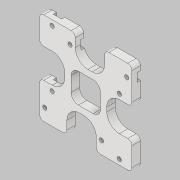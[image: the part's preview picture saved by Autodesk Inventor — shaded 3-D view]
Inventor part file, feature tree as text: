
AUTODESK INVENTOR PART (.ipt)
format: ipt  version: 2019.2 (Build 232265000, 265)  size: 918,016 bytes
history: native  units: mm
features: fillet x4, other x2, extrude x2, sketch x2
ambient origin geometry x8: Origin, YZ Plane, XZ Plane, XY Plane, X Axis, Y Axis, Z Axis, Center Point
bodies: Body1 (feature_tree)
feature tree (10):
  other  "BaseBottom"
  extrude  "Base"  Depth=12.0mm
  fillet  "Rundung1"  Radius=5.0mm
  fillet  "Rundung2"  Radius=14.0mm
  extrude  "Extrusion3"  Depth=3.0mm
  fillet  "Rundung3"  Radius=4.0mm
  fillet  "Rundung4"  Radius=3.5mm
  sketch  "Skizze2"  dims[d9=32.0mm d10=12.0mm d11=5.0mm d12=14.0mm]
  sketch  "Skizze4"  dims[d13=2.0mm d14=32.0mm d15=12.0mm d16=5.0mm d17=14.0mm d18=2.0mm d19=32.0mm d20=12.0mm d21=5.0mm d22=14.0mm d23=2.0mm d24=32.0mm d25=12.0mm d26=5.0mm d27=14.0mm d28=2.0mm d29=3.0mm d30=4.0mm d31=0.0mm d32=3.5mm d33=6.0mm d45=4.0mm d46=4.0mm d47=4.0mm d48=1.5mm d49=0.0mm d50=4.0mm d51=4.0mm d52=4.0mm d53=4.0mm d54=4.0mm d55=4.0mm d56=4.0mm d57=4.0mm d58=2.0mm d59=0.25mm]
  other  "BasePlate"
